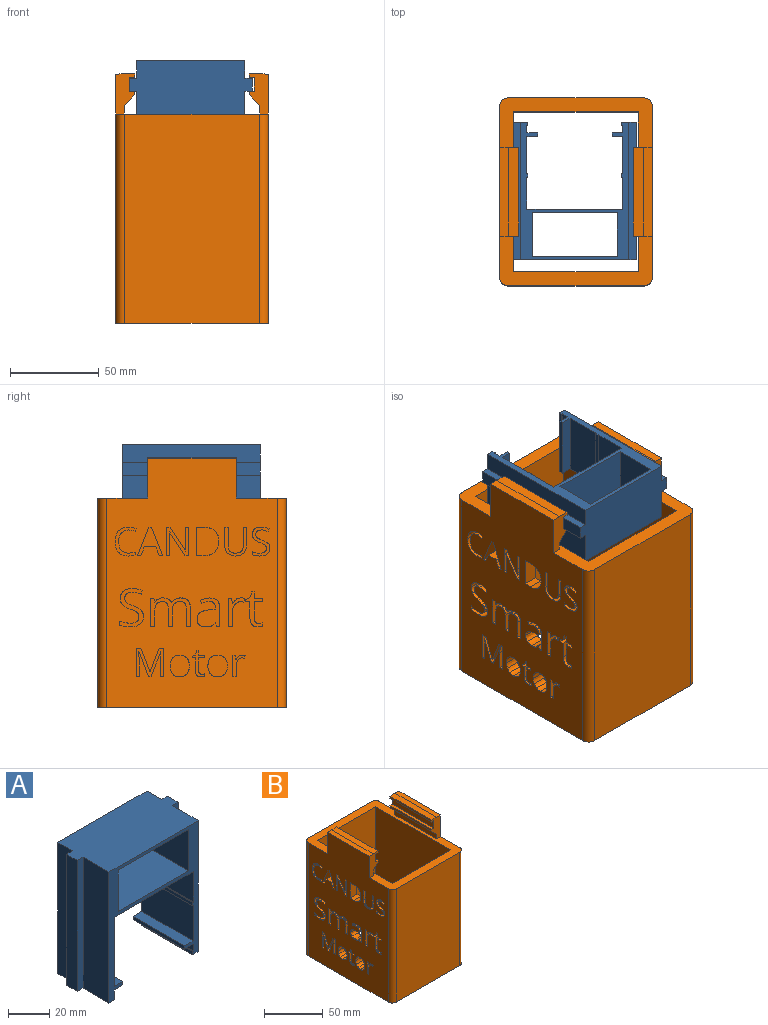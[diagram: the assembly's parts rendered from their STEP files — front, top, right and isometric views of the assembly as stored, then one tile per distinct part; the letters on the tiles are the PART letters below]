
ASSEMBLY  parts=2 mates=2
PART A: 42 faces, bbox 69x35x77.5 mm
  f0: plane 77.5x10mm, normal (1,0,0), area 775mm2, adj f16,f18,f35,f41
  f1: plane 77.5x10mm, normal (-1,0,0), area 775mm2, adj f18,f20,f35,f37
  f2: plane 35x0.5mm, normal (0,0,1), area 17.5mm2, adj f3,f33,f34,f35
  f3: plane 35x18mm, normal (1,0,0), area 630mm2, adj f2,f4,f34,f35
  f4: plane 54x35mm, normal (0,0,-1), area 1890mm2, adj f3,f5,f34,f35
  f5: plane 35x18mm, normal (-1,0,0), area 630mm2, adj f4,f6,f34,f35
  f6: plane 35x0.5mm, normal (0,0,1), area 17.5mm2, adj f5,f7,f34,f35
  f7: plane 35x2mm, normal (-1,0,0), area 70mm2, adj f6,f8,f34,f35
  f8: plane 35x0.5mm, normal (0,0,-1), area 17.5mm2, adj f7,f9,f34,f35
  f9: plane 35x21mm, normal (-1,0,0), area 735mm2, adj f8,f10,f34,f35
  f10: plane 35x6mm, normal (0,0,1), area 210mm2, adj f9,f11,f34,f35
  f11: plane 35x2mm, normal (-1,0,0), area 70mm2, adj f10,f12,f34,f35
  f12: plane 35x6mm, normal (0,0,-1), area 210mm2, adj f11,f13,f34,f35
  f13: plane 35x4mm, normal (-1,0,0), area 140mm2, adj f12,f14,f34,f35
  f14: plane 35x0.5mm, normal (0,0,1), area 17.5mm2, adj f13,f15,f34,f35
  f15: plane 35x2mm, normal (-1,0,0), area 70mm2, adj f14,f16,f34,f35
  f16: plane 35x8mm, normal (0,0,-1), area 169.2mm2, adj f0,f15,f17,f34,f35,f39,f40,f41
  f17: plane 77.5x17.7mm, normal (1,0,0), area 1371.8mm2, adj f16,f18,f34,f39
  f18: plane 69x35mm, normal (0,0,1), area 2193.4mm2, adj f0,f1,f17,f19,f34,f35,f36,f37
  f19: plane 77.5x17.7mm, normal (-1,0,0), area 1371.8mm2, adj f18,f20,f34,f36
  f20: plane 35x8mm, normal (0,0,-1), area 169.2mm2, adj f1,f19,f21,f34,f35,f36,f37,f38
  f21: plane 35x2mm, normal (1,0,0), area 70mm2, adj f20,f22,f34,f35
  f22: plane 35x0.5mm, normal (0,0,1), area 17.5mm2, adj f21,f23,f34,f35
  f23: plane 35x4mm, normal (1,0,0), area 140mm2, adj f22,f24,f34,f35
  f24: plane 35x6mm, normal (0,0,-1), area 210mm2, adj f23,f25,f34,f35
  f25: plane 35x2mm, normal (1,0,0), area 70mm2, adj f24,f26,f34,f35
  f26: plane 35x6mm, normal (0,0,1), area 210mm2, adj f25,f27,f34,f35
  f27: plane 35x21mm, normal (1,0,0), area 735mm2, adj f26,f28,f34,f35
  f28: plane 35x0.5mm, normal (0,0,-1), area 17.5mm2, adj f27,f33,f34,f35
  f29: plane 35x24.5mm, normal (-1,0,0), area 857.5mm2, adj f30,f32,f34,f35
  f30: plane 48x35mm, normal (0,0,1), area 1680mm2, adj f29,f31,f34,f35
  f31: plane 35x24.5mm, normal (1,0,0), area 857.5mm2, adj f30,f32,f34,f35
  f32: plane 48x35mm, normal (0,0,-1), area 1680mm2, adj f29,f31,f34,f35
  f33: plane 35x2mm, normal (1,0,0), area 70mm2, adj f2,f28,f34,f35
  f34: plane 77.5x61mm, normal (0,-1,0), area 933.5mm2, adj f2,f3,f4,f5,f6,f7,f8,f9
  f35: plane 77.5x61mm, normal (0,1,0), area 933.5mm2, adj f0,f1,f2,f3,f4,f5,f6,f7
  f36: plane 77.5x4mm, normal (0,-1,0), area 310mm2, adj f18,f19,f20,f38
  f37: plane 77.5x4mm, normal (0,1,0), area 310mm2, adj f1,f18,f20,f38
  f38: plane 77.5x7.3mm, normal (-1,0,0), area 565.8mm2, adj f18,f20,f36,f37
  f39: plane 77.5x4mm, normal (0,-1,0), area 310mm2, adj f16,f17,f18,f40
  f40: plane 77.5x7.3mm, normal (1,0,0), area 565.7mm2, adj f16,f18,f39,f41
  f41: plane 77.5x4mm, normal (0,1,0), area 310mm2, adj f0,f16,f18,f40
PART B: 292 faces, bbox 86x106x140.6 mm
  f0: plane 140.5x96mm, normal (-1,0,0), area 11035.3mm2, adj f2,f4,f5,f13,f29,f32,f33,f36
  f1: plane 118x90mm, normal (1,0,0), area 9202.5mm2, adj f2,f10,f11,f13,f36,f37,f38,f39
  f2: plane 106x86mm, normal (0,0,1), area 2309.5mm2, adj f0,f1,f3,f4,f5,f6,f7,f8
  f3: plane 118x76mm, normal (0,1,0), area 8968mm2, adj f2,f4,f12,f13
  f4: cylinder r=5mm len=118mm, axis (0,0,-1), area 926.8mm2, adj f0,f2,f3,f13
  f5: cylinder r=5mm len=118mm, axis (0,0,-1), area 926.8mm2, adj f0,f2,f6,f13
  f6: plane 118x76mm, normal (0,-1,0), area 8968mm2, adj f2,f5,f7,f13
  f7: cylinder r=5mm len=118mm, axis (0,0,-1), area 926.8mm2, adj f2,f6,f8,f13
  f8: plane 140.5x96mm, normal (1,0,0), area 12452.8mm2, adj f2,f7,f12,f13,f16,f22,f23
  f9: plane 118x90mm, normal (-1,0,0), area 10620mm2, adj f2,f10,f11,f13
  f10: plane 118x70mm, normal (0,1,0), area 8260mm2, adj f1,f2,f9,f13
  f11: plane 118x70mm, normal (0,-1,0), area 8260mm2, adj f1,f2,f9,f13
  f12: cylinder r=5mm len=118mm, axis (0,0,-1), area 926.8mm2, adj f2,f3,f8,f13
  f13: plane 106x86mm, normal (0,0,-1), area 2794.5mm2, adj f0,f1,f3,f4,f5,f6,f7,f8
  f14: plane 50x2mm, normal (-1,0,0), area 100mm2, adj f21,f22,f23,f34
  f15: plane 50x4.8mm, normal (-1,0,0), area 240mm2, adj f2,f22,f23,f34
  f16: plane 50x4.85mm, normal (0.02,0,1), area 242.6mm2, adj f8,f17,f22,f23
  f17: plane 50x6mm, normal (0,0,1), area 300mm2, adj f16,f18,f22,f23
  f18: plane 50x2mm, normal (-1,0,0), area 100mm2, adj f17,f19,f22,f23
  f19: plane 50x3mm, normal (0,0,-1), area 150mm2, adj f18,f20,f22,f23
  f20: plane 50x7.8mm, normal (-1,0,0), area 390mm2, adj f19,f21,f22,f23
  f21: plane 50x3mm, normal (0,0,1), area 150mm2, adj f14,f20,f22,f23
  f22: plane 22.6x10.85mm, normal (0,-1,0), area 174.8mm2, adj f2,f8,f14,f15,f16,f17,f18,f19
  f23: plane 22.6x10.85mm, normal (0,1,0), area 174.8mm2, adj f2,f8,f14,f15,f16,f17,f18,f19
  f24: plane 50x3mm, normal (0,0,1), area 150mm2, adj f25,f31,f32,f33
  f25: plane 50x7.8mm, normal (1,0,0), area 390mm2, adj f24,f26,f32,f33
  f26: plane 50x3mm, normal (0,0,-1), area 150mm2, adj f25,f27,f32,f33
  f27: plane 50x2mm, normal (1,0,0), area 100mm2, adj f26,f28,f32,f33
  f28: plane 50x6mm, normal (0,0,1), area 300mm2, adj f27,f29,f32,f33
  f29: plane 50x4.85mm, normal (-0.02,0,1), area 242.6mm2, adj f0,f28,f32,f33
  f30: plane 50x4.8mm, normal (1,0,0), area 240mm2, adj f2,f32,f33,f35
  f31: plane 50x2mm, normal (1,0,0), area 100mm2, adj f24,f32,f33,f35
  f32: plane 22.6x10.85mm, normal (0,-1,0), area 174.8mm2, adj f0,f2,f24,f25,f26,f27,f28,f29
  f33: plane 22.6x10.85mm, normal (0,1,0), area 174.8mm2, adj f0,f2,f24,f25,f26,f27,f28,f29
  f34: plane 50x6mm, normal (-0.71,0,-0.71), area 424.3mm2, adj f14,f15,f22,f23
  f35: plane 50x6mm, normal (0.71,0,-0.71), area 424.3mm2, adj f30,f31,f32,f33
  f36: extruded ~8x4.14mm, area 37.1mm2, adj f0,f1,f37,f50
  f37: extruded ~8x3.61mm, area 29.9mm2, adj f0,f1,f36,f38
  f38: plane 8x1.59mm, normal (0,0.9,0.44), area 14.2mm2, adj f0,f1,f37,f39
  f39: extruded ~8x4.37mm, area 36mm2, adj f0,f1,f38,f40
  f40: extruded ~8x4.08mm, area 34mm2, adj f0,f1,f39,f41
  f41: extruded ~8x2.85mm, area 31.6mm2, adj f0,f1,f40,f42
  f42: extruded ~8x4.31mm, area 35.5mm2, adj f0,f1,f41,f43
  f43: extruded ~8x6.06mm, area 52mm2, adj f0,f1,f42,f44
  f44: extruded ~8x5.42mm, area 48.1mm2, adj f0,f1,f43,f45
  f45: extruded ~8x4.08mm, area 33.2mm2, adj f0,f1,f44,f46
  f46: plane 8x1.62mm, normal (0,1,0), area 12.9mm2, adj f0,f1,f45,f47
  f47: extruded ~8x3.8mm, area 30.8mm2, adj f0,f1,f46,f48
  f48: extruded ~8x4.17mm, area 37.3mm2, adj f0,f1,f47,f49
  f49: extruded ~8x4.82mm, area 41.2mm2, adj f0,f1,f48,f50
  f50: extruded ~8x4.78mm, area 41mm2, adj f0,f1,f36,f49
  f51: extruded ~8x0.93mm, area 7.4mm2, adj f0,f1,f52,f69
  f52: extruded ~8x1.4mm, area 12.5mm2, adj f0,f1,f51,f53
  f53: extruded ~8x1.65mm, area 14.1mm2, adj f0,f1,f52,f54
  f54: plane 8x7.01mm, normal (0,1,0), area 56.1mm2, adj f0,f1,f53,f55
  f55: plane 8x3.46mm, normal (0,0,1), area 27.7mm2, adj f0,f1,f54,f56
  f56: plane 8x1.4mm, normal (0,1,0), area 11.2mm2, adj f0,f1,f55,f57
  f57: plane 8x3.46mm, normal (0,0,-1), area 27.7mm2, adj f0,f1,f56,f58
  f58: plane 8x2.76mm, normal (0,1,0), area 22.1mm2, adj f0,f1,f57,f59
  f59: plane 8x1.04mm, normal (0,0,-1), area 8.3mm2, adj f0,f1,f58,f60
  f60: plane 8x2.54mm, normal (0,-0.96,-0.29), area 21.2mm2, adj f0,f1,f59,f61
  f61: plane 8x1.71mm, normal (0,-0.4,-0.92), area 14.9mm2, adj f0,f1,f60,f62
  f62: plane 8x0.87mm, normal (0,-1,0), area 7mm2, adj f0,f1,f61,f63
  f63: plane 8x1.71mm, normal (0,0,1), area 13.7mm2, adj f0,f1,f62,f64
  f64: plane 8x7.09mm, normal (0,-1,0), area 56.7mm2, adj f0,f1,f63,f65
  f65: extruded ~8x3.64mm, area 46.1mm2, adj f0,f1,f64,f66
  f66: extruded ~8x1.03mm, area 8.3mm2, adj f0,f1,f65,f67
  f67: extruded ~8x0.86mm, area 7.2mm2, adj f0,f1,f66,f68
  f68: plane 8x1.38mm, normal (0,1,0), area 11mm2, adj f0,f1,f67,f69
  f69: extruded ~8x0.71mm, area 5.8mm2, adj f0,f1,f51,f68
  f70: extruded ~8x1.42mm, area 11.5mm2, adj f0,f1,f71,f82
  f71: extruded ~8x2.06mm, area 17.5mm2, adj f0,f1,f70,f72
  f72: extruded ~8x1.79mm, area 19.4mm2, adj f0,f1,f71,f73
  f73: plane 8x0.09mm, normal (0,0,-1), area 0.7mm2, adj f0,f1,f72,f74
  f74: plane 8x2.21mm, normal (0,1,-0.09), area 17.7mm2, adj f0,f1,f73,f75
  f75: plane 8x1.49mm, normal (0,0,-1), area 11.9mm2, adj f0,f1,f74,f76
  f76: plane 11.91x8mm, normal (0,-1,0), area 95.3mm2, adj f0,f1,f75,f77
  f77: plane 8x1.81mm, normal (0,0,1), area 14.4mm2, adj f0,f1,f76,f78
  f78: plane 8x6.39mm, normal (0,1,0), area 51.2mm2, adj f0,f1,f77,f79
  f79: extruded ~8x2.92mm, area 25.4mm2, adj f0,f1,f78,f80
  f80: extruded ~8x2.47mm, area 22.6mm2, adj f0,f1,f79,f81
  f81: extruded ~8x1.3mm, area 10.5mm2, adj f0,f1,f80,f82
  f82: plane 8x1.67mm, normal (0,0.99,0.15), area 13.5mm2, adj f0,f1,f70,f81
  f83: plane 8x5.06mm, normal (0,-0.93,0.36), area 43.4mm2, adj f0,f1,f84,f90
  f84: plane 8x1.91mm, normal (0,0,1), area 15.3mm2, adj f0,f1,f83,f85
  f85: plane 15.97x8mm, normal (0,0.93,-0.36), area 137.2mm2, adj f0,f1,f84,f86
  f86: plane 8x1.56mm, normal (0,0,-1), area 12.4mm2, adj f0,f1,f85,f87
  f87: plane 15.97x8mm, normal (0,-0.93,-0.37), area 137.3mm2, adj f0,f1,f86,f88
  f88: plane 8x1.87mm, normal (0,0,1), area 15mm2, adj f0,f1,f87,f89
  f89: plane 8x5.06mm, normal (0,0.93,0.36), area 43.4mm2, adj f0,f1,f88,f90
  f90: plane 8x6.37mm, normal (0,0,1), area 51mm2, adj f0,f1,f83,f89
  f91: extruded ~8x6.02mm, area 52.5mm2, adj f0,f1,f92,f97
  f92: extruded ~8x5.74mm, area 50.1mm2, adj f0,f1,f91,f93
  f93: extruded ~8x5.77mm, area 50.3mm2, adj f0,f1,f92,f94
  f94: plane 8x4.87mm, normal (0,0,-1), area 39mm2, adj f0,f1,f93,f95
  f95: plane 15.9x8mm, normal (0,-1,0), area 127.2mm2, adj f0,f1,f94,f96
  f96: plane 8x4.41mm, normal (0,0,1), area 35.2mm2, adj f0,f1,f95,f97
  f97: extruded ~8x6.15mm, area 53.3mm2, adj f0,f1,f91,f96
  f98: extruded ~8x4.55mm, area 39.1mm2, adj f0,f1,f99,f106
  f99: extruded ~8x4.5mm, area 38.7mm2, adj f0,f1,f98,f100
  f100: extruded ~8x3.97mm, area 35.6mm2, adj f0,f1,f99,f101
  f101: extruded ~8x4.05mm, area 36mm2, adj f0,f1,f100,f102
  f102: extruded ~8x4.54mm, area 39mm2, adj f0,f1,f101,f103
  f103: extruded ~8x3.28mm, area 27mm2, adj f0,f1,f102,f104
  f104: extruded ~8x2.15mm, area 23.4mm2, adj f0,f1,f103,f105
  f105: extruded ~8x2.84mm, area 23.8mm2, adj f0,f1,f104,f106
  f106: extruded ~8x4.05mm, area 36.1mm2, adj f0,f1,f98,f105
  f107: extruded ~8x4.55mm, area 39.1mm2, adj f0,f1,f108,f115
  f108: extruded ~8x4.5mm, area 38.7mm2, adj f0,f1,f107,f109
  f109: extruded ~8x3.97mm, area 35.6mm2, adj f0,f1,f108,f110
  f110: extruded ~8x4.05mm, area 36mm2, adj f0,f1,f109,f111
  f111: extruded ~8x4.54mm, area 39mm2, adj f0,f1,f110,f112
  f112: extruded ~8x3.28mm, area 27mm2, adj f0,f1,f111,f113
  f113: extruded ~8x2.15mm, area 23.4mm2, adj f0,f1,f112,f114
  f114: extruded ~8x2.84mm, area 23.8mm2, adj f0,f1,f113,f115
  f115: extruded ~8x4.05mm, area 36.1mm2, adj f0,f1,f107,f114
  f116: plane 8x2.25mm, normal (0,-0.98,0.21), area 18.4mm2, adj f0,f1,f117,f134
  f117: plane 8x1.78mm, normal (0,0,1), area 14.2mm2, adj f0,f1,f116,f118
  f118: plane 10.79x8mm, normal (0,1,0), area 86.3mm2, adj f0,f1,f117,f119
  f119: extruded ~8x4.02mm, area 35mm2, adj f0,f1,f118,f120
  f120: extruded ~8x4.19mm, area 35.8mm2, adj f0,f1,f119,f121
  f121: extruded ~8x2.79mm, area 22.6mm2, adj f0,f1,f120,f122
  f122: extruded ~8x2.56mm, area 22mm2, adj f0,f1,f121,f123
  f123: plane 8x1.83mm, normal (0,-0.93,0.37), area 15.8mm2, adj f0,f1,f122,f124
  f124: extruded ~8x4.47mm, area 37.3mm2, adj f0,f1,f123,f125
  f125: extruded ~8x2.56mm, area 22.3mm2, adj f0,f1,f124,f126
  f126: extruded ~8x2.75mm, area 23.4mm2, adj f0,f1,f125,f127
  f127: plane 8x0.98mm, normal (0,-1,0), area 7.9mm2, adj f0,f1,f126,f128
  f128: plane 8x2.68mm, normal (0,-0.03,-1), area 21.5mm2, adj f0,f1,f127,f129
  f129: extruded ~8x7.65mm, area 82.3mm2, adj f0,f1,f128,f130
  f130: extruded ~8x3.45mm, area 30.5mm2, adj f0,f1,f129,f131
  f131: extruded ~8x3.68mm, area 31.7mm2, adj f0,f1,f130,f132
  f132: extruded ~8x2.94mm, area 24mm2, adj f0,f1,f131,f133
  f133: extruded ~8x2.36mm, area 25mm2, adj f0,f1,f132,f134
  f134: plane 8x0.12mm, normal (0,0,1), area 0.9mm2, adj f0,f1,f116,f133
  f135: extruded ~8x4.34mm, area 39.8mm2, adj f0,f1,f136,f159
  f136: extruded ~8x3.52mm, area 30.6mm2, adj f0,f1,f135,f137
  f137: extruded ~8x4.56mm, area 42.1mm2, adj f0,f1,f136,f138
  f138: extruded ~8x2.93mm, area 25.7mm2, adj f0,f1,f137,f139
  f139: extruded ~8x1.36mm, area 15.1mm2, adj f0,f1,f138,f140
  f140: extruded ~8x1.79mm, area 14.9mm2, adj f0,f1,f139,f141
  f141: extruded ~8x2.32mm, area 21.3mm2, adj f0,f1,f140,f142
  f142: extruded ~8x3.04mm, area 25.7mm2, adj f0,f1,f141,f143
  f143: extruded ~8x5.08mm, area 41.8mm2, adj f0,f1,f142,f144
  f144: plane 8x2.13mm, normal (0,0.94,0.34), area 18.1mm2, adj f0,f1,f143,f145
  f145: extruded ~8x5.78mm, area 47.5mm2, adj f0,f1,f144,f146
  f146: extruded ~8x4.85mm, area 41.2mm2, adj f0,f1,f145,f147
  f147: extruded ~8x3.88mm, area 35.6mm2, adj f0,f1,f146,f148
  f148: extruded ~8x3.76mm, area 32.5mm2, adj f0,f1,f147,f149
  f149: extruded ~8x4.2mm, area 39.5mm2, adj f0,f1,f148,f150
  f150: extruded ~8x3.14mm, area 27.3mm2, adj f0,f1,f149,f151
  f151: extruded ~8x1.47mm, area 15.8mm2, adj f0,f1,f150,f152
  f152: extruded ~8x1.79mm, area 15mm2, adj f0,f1,f151,f153
  f153: extruded ~8x2.59mm, area 23.9mm2, adj f0,f1,f152,f154
  f154: extruded ~8x3.69mm, area 31mm2, adj f0,f1,f153,f155
  f155: extruded ~8x3.03mm, area 24.4mm2, adj f0,f1,f154,f156
  f156: extruded ~8x2.83mm, area 23.7mm2, adj f0,f1,f155,f157
  f157: plane 8x2.36mm, normal (0,-1,0), area 18.9mm2, adj f0,f1,f156,f158
  f158: extruded ~8x5.77mm, area 47.1mm2, adj f0,f1,f157,f159
  f159: extruded ~8x5.48mm, area 46.4mm2, adj f0,f1,f135,f158
  f160: extruded ~8x3.28mm, area 30mm2, adj f0,f1,f161,f184
  f161: extruded ~8x2.65mm, area 23.1mm2, adj f0,f1,f160,f162
  f162: extruded ~8x3.44mm, area 31.8mm2, adj f0,f1,f161,f163
  f163: extruded ~8x2.21mm, area 19.4mm2, adj f0,f1,f162,f164
  f164: extruded ~8x1.03mm, area 11.4mm2, adj f0,f1,f163,f165
  f165: extruded ~8x1.35mm, area 11.2mm2, adj f0,f1,f164,f166
  f166: extruded ~8x1.75mm, area 16.1mm2, adj f0,f1,f165,f167
  f167: extruded ~8x2.3mm, area 19.4mm2, adj f0,f1,f166,f168
  f168: extruded ~8x3.83mm, area 31.5mm2, adj f0,f1,f167,f169
  f169: plane 8x1.61mm, normal (0,0.94,0.34), area 13.7mm2, adj f0,f1,f168,f170
  f170: extruded ~8x4.36mm, area 35.8mm2, adj f0,f1,f169,f171
  f171: extruded ~8x3.66mm, area 31.1mm2, adj f0,f1,f170,f172
  f172: extruded ~8x2.93mm, area 26.9mm2, adj f0,f1,f171,f173
  f173: extruded ~8x2.84mm, area 24.5mm2, adj f0,f1,f172,f174
  f174: extruded ~8x3.17mm, area 29.8mm2, adj f0,f1,f173,f175
  f175: extruded ~8x2.37mm, area 20.6mm2, adj f0,f1,f174,f176
  f176: extruded ~8x1.11mm, area 11.9mm2, adj f0,f1,f175,f177
  f177: extruded ~8x1.35mm, area 11.3mm2, adj f0,f1,f176,f178
  f178: extruded ~8x1.95mm, area 18mm2, adj f0,f1,f177,f179
  f179: extruded ~8x2.78mm, area 23.4mm2, adj f0,f1,f178,f180
  f180: extruded ~8x2.28mm, area 18.4mm2, adj f0,f1,f179,f181
  f181: extruded ~8x2.13mm, area 17.9mm2, adj f0,f1,f180,f182
  f182: plane 8x1.78mm, normal (0,-1,0), area 14.3mm2, adj f0,f1,f181,f183
  f183: extruded ~8x4.35mm, area 35.6mm2, adj f0,f1,f182,f184
  f184: extruded ~8x4.13mm, area 35mm2, adj f0,f1,f160,f183
  f185: plane 10.29x8mm, normal (0,1,0), area 82.3mm2, adj f0,f1,f186,f198
  f186: plane 8x1.85mm, normal (0,0,-1), area 14.8mm2, adj f0,f1,f185,f187
  f187: plane 10.35x8mm, normal (0,-1,0), area 82.8mm2, adj f0,f1,f186,f188
  f188: extruded ~8x3.07mm, area 26.8mm2, adj f0,f1,f187,f189
  f189: extruded ~8x3.1mm, area 26.9mm2, adj f0,f1,f188,f190
  f190: extruded ~8x3.2mm, area 27.7mm2, adj f0,f1,f189,f191
  f191: extruded ~8x3.06mm, area 26.7mm2, adj f0,f1,f190,f192
  f192: plane 10.38x8mm, normal (0,1,0), area 83mm2, adj f0,f1,f191,f193
  f193: plane 8x1.85mm, normal (0,0,-1), area 14.8mm2, adj f0,f1,f192,f194
  f194: plane 10.25x8mm, normal (0,-1,0), area 82mm2, adj f0,f1,f193,f195
  f195: extruded ~8x4.31mm, area 37.7mm2, adj f0,f1,f194,f196
  f196: extruded ~8x4.44mm, area 38.7mm2, adj f0,f1,f195,f197
  f197: extruded ~8x4.51mm, area 39.2mm2, adj f0,f1,f196,f198
  f198: extruded ~8x4.28mm, area 37.7mm2, adj f0,f1,f185,f197
  f199: plane 8x2.11mm, normal (0,0,1), area 16.9mm2, adj f0,f1,f200,f213
  f200: plane 15.9x8mm, normal (0,1,0), area 127.2mm2, adj f0,f1,f199,f201
  f201: plane 8x1.73mm, normal (0,0,-1), area 13.8mm2, adj f0,f1,f200,f202
  f202: plane 9.13x8mm, normal (0,-1,0), area 73mm2, adj f0,f1,f201,f203
  f203: extruded ~8x2.28mm, area 18.2mm2, adj f0,f1,f202,f204
  f204: extruded ~8x1.89mm, area 15.1mm2, adj f0,f1,f203,f205
  f205: plane 8x0.09mm, normal (0,0,-1), area 0.7mm2, adj f0,f1,f204,f206
  f206: plane 13.29x8.67mm, normal (0,0.84,-0.55), area 127mm2, adj f0,f1,f205,f207
  f207: plane 8x2.09mm, normal (0,0,-1), area 16.7mm2, adj f0,f1,f206,f208
  f208: plane 15.9x8mm, normal (0,-1,0), area 127.2mm2, adj f0,f1,f207,f209
  f209: plane 8x1.71mm, normal (0,0,1), area 13.7mm2, adj f0,f1,f208,f210
  f210: plane 9.04x8mm, normal (0,1,0), area 72.3mm2, adj f0,f1,f209,f211
  f211: extruded ~8x4.31mm, area 34.5mm2, adj f0,f1,f210,f212
  f212: plane 8x0.09mm, normal (0,0,1), area 0.7mm2, adj f0,f1,f211,f213
  f213: plane 13.34x8.69mm, normal (0,-0.84,0.55), area 127.4mm2, adj f0,f1,f199,f212
  f214: plane 14.09x8mm, normal (0,-0.93,0.36), area 120.7mm2, adj f0,f1,f215,f231
  f215: plane 8x1.49mm, normal (0,0,1), area 11.9mm2, adj f0,f1,f214,f216
  f216: plane 14.07x8mm, normal (0,0.93,0.36), area 120.7mm2, adj f0,f1,f215,f217
  f217: plane 8x0.09mm, normal (0,0,1), area 0.7mm2, adj f0,f1,f216,f218
  f218: extruded ~8x3.83mm, area 30.6mm2, adj f0,f1,f217,f219
  f219: plane 10.24x8mm, normal (0,-1,0), area 81.9mm2, adj f0,f1,f218,f220
  f220: plane 8x1.85mm, normal (0,0,1), area 14.8mm2, adj f0,f1,f219,f221
  f221: plane 15.89x8mm, normal (0,1,0), area 127.2mm2, adj f0,f1,f220,f222
  f222: plane 8x2.76mm, normal (0,0,-1), area 22.1mm2, adj f0,f1,f221,f223
  f223: plane 13.11x8mm, normal (0,-0.93,-0.36), area 112.5mm2, adj f0,f1,f222,f224
  f224: plane 8x0.09mm, normal (0,0,-1), area 0.7mm2, adj f0,f1,f223,f225
  f225: plane 13.11x8mm, normal (0,0.93,-0.36), area 112.4mm2, adj f0,f1,f224,f226
  f226: plane 8x2.78mm, normal (0,0,-1), area 22.3mm2, adj f0,f1,f225,f227
  f227: plane 15.89x8mm, normal (0,-1,0), area 127.2mm2, adj f0,f1,f226,f228
  f228: plane 8x1.71mm, normal (0,0,1), area 13.7mm2, adj f0,f1,f227,f229
  f229: plane 10.11x8mm, normal (0,1,0), area 80.9mm2, adj f0,f1,f228,f230
  f230: extruded ~8x3.98mm, area 31.9mm2, adj f0,f1,f229,f231
  f231: plane 8x0.09mm, normal (0,0,1), area 0.7mm2, adj f0,f1,f214,f230
  f232: extruded ~8x1.23mm, area 9.9mm2, adj f0,f1,f233,f250
  f233: extruded ~8x1.86mm, area 16.6mm2, adj f0,f1,f232,f234
  f234: extruded ~8x2.19mm, area 18.7mm2, adj f0,f1,f233,f235
  f235: plane 9.3x8mm, normal (0,1,0), area 74.4mm2, adj f0,f1,f234,f236
  f236: plane 8x4.59mm, normal (0,0,1), area 36.7mm2, adj f0,f1,f235,f237
  f237: plane 8x1.86mm, normal (0,1,0), area 14.9mm2, adj f0,f1,f236,f238
  f238: plane 8x4.59mm, normal (0,0,-1), area 36.7mm2, adj f0,f1,f237,f239
  f239: plane 8x3.66mm, normal (0,1,0), area 29.3mm2, adj f0,f1,f238,f240
  f240: plane 8x1.38mm, normal (0,0,-1), area 11.1mm2, adj f0,f1,f239,f241
  f241: plane 8x3.37mm, normal (0,-0.96,-0.29), area 28.2mm2, adj f0,f1,f240,f242
  f242: plane 8x2.27mm, normal (0,-0.4,-0.92), area 19.8mm2, adj f0,f1,f241,f243
  f243: plane 8x1.15mm, normal (0,-1,0), area 9.2mm2, adj f0,f1,f242,f244
  f244: plane 8x2.27mm, normal (0,0,1), area 18.1mm2, adj f0,f1,f243,f245
  f245: plane 9.4x8mm, normal (0,-1,0), area 75.2mm2, adj f0,f1,f244,f246
  f246: extruded ~8x4.83mm, area 61.1mm2, adj f0,f1,f245,f247
  f247: extruded ~8x1.37mm, area 11mm2, adj f0,f1,f246,f248
  f248: extruded ~8x1.14mm, area 9.5mm2, adj f0,f1,f247,f249
  f249: plane 8x1.83mm, normal (0,1,0), area 14.7mm2, adj f0,f1,f248,f250
  f250: extruded ~8x0.94mm, area 7.7mm2, adj f0,f1,f232,f249
  f251: extruded ~8x1.89mm, area 15.2mm2, adj f0,f1,f252,f263
  f252: extruded ~8x2.73mm, area 23.2mm2, adj f0,f1,f251,f253
  f253: extruded ~8x2.38mm, area 25.7mm2, adj f0,f1,f252,f254
  f254: plane 8x0.12mm, normal (0,0,-1), area 0.9mm2, adj f0,f1,f253,f255
  f255: plane 8x2.93mm, normal (0,1,-0.09), area 23.5mm2, adj f0,f1,f254,f256
  f256: plane 8x1.97mm, normal (0,0,-1), area 15.8mm2, adj f0,f1,f255,f257
  f257: plane 15.8x8mm, normal (0,-1,0), area 126.4mm2, adj f0,f1,f256,f258
  f258: plane 8x2.39mm, normal (0,0,1), area 19.2mm2, adj f0,f1,f257,f259
  f259: plane 8.48x8mm, normal (0,1,0), area 67.8mm2, adj f0,f1,f258,f260
  f260: extruded ~8x3.88mm, area 33.6mm2, adj f0,f1,f259,f261
  f261: extruded ~8x3.28mm, area 30mm2, adj f0,f1,f260,f262
  f262: extruded ~8x1.73mm, area 14mm2, adj f0,f1,f261,f263
  f263: plane 8x2.22mm, normal (0,0.99,0.15), area 18mm2, adj f0,f1,f251,f262
  f264: plane 10.28x8mm, normal (0,-1,0), area 82.2mm2, adj f0,f1,f265,f291
  f265: plane 8x2.39mm, normal (0,0,1), area 19.1mm2, adj f0,f1,f264,f266
  f266: plane 10.31x8mm, normal (0,1,0), area 82.5mm2, adj f0,f1,f265,f267
  f267: extruded ~8x4.41mm, area 37.8mm2, adj f0,f1,f266,f268
  f268: extruded ~8x4.01mm, area 34.9mm2, adj f0,f1,f267,f269
  f269: extruded ~8x3.06mm, area 25.4mm2, adj f0,f1,f268,f270
  f270: extruded ~8x2.05mm, area 23mm2, adj f0,f1,f269,f271
  f271: plane 8x0.12mm, normal (0,0,-1), area 0.9mm2, adj f0,f1,f270,f272
  f272: extruded ~8x4.84mm, area 47.3mm2, adj f0,f1,f271,f273
  f273: extruded ~8x2.76mm, area 22.9mm2, adj f0,f1,f272,f274
  f274: extruded ~8x1.91mm, area 21.3mm2, adj f0,f1,f273,f275
  f275: plane 8x0.12mm, normal (0,0,-1), area 0.9mm2, adj f0,f1,f274,f276
  f276: plane 8x2.16mm, normal (0,0.98,-0.18), area 17.6mm2, adj f0,f1,f275,f277
  f277: plane 8x1.95mm, normal (0,0,-1), area 15.6mm2, adj f0,f1,f276,f278
  f278: plane 15.8x8mm, normal (0,-1,0), area 126.4mm2, adj f0,f1,f277,f279
  f279: plane 8x2.39mm, normal (0,0,1), area 19.2mm2, adj f0,f1,f278,f280
  f280: plane 8.29x8mm, normal (0,1,0), area 66.3mm2, adj f0,f1,f279,f281
  f281: extruded ~8x4.42mm, area 36.9mm2, adj f0,f1,f280,f282
  f282: extruded ~8x3.29mm, area 29.5mm2, adj f0,f1,f281,f283
  f283: extruded ~8x2.52mm, area 22.3mm2, adj f0,f1,f282,f284
  f284: extruded ~8x2.84mm, area 24.1mm2, adj f0,f1,f283,f285
  f285: plane 10.28x8mm, normal (0,-1,0), area 82.2mm2, adj f0,f1,f284,f286
  f286: plane 8x2.39mm, normal (0,0,1), area 19.2mm2, adj f0,f1,f285,f287
  f287: plane 8.83x8mm, normal (0,1,0), area 70.6mm2, adj f0,f1,f286,f288
  f288: extruded ~8x3.95mm, area 33.4mm2, adj f0,f1,f287,f289
  f289: extruded ~8x3.3mm, area 29.3mm2, adj f0,f1,f288,f290
  f290: extruded ~8x2.51mm, area 22.2mm2, adj f0,f1,f289,f291
  f291: extruded ~8x2.84mm, area 24.1mm2, adj f0,f1,f264,f290
PLACE A rot(axis=(1,0,0),90deg) t=(-31.78,23.17,150.71)mm
PLACE B t=(-23.13,-29.95,12.61)mm fixed
MATE planar A.f36 <-> B.f24  axis (0,0,-1) through (-91.28,15.42,133.41)mm
MATE planar A.f38 <-> B.f25  axis (-1,0,0) through (-93.28,15.42,137.06)mm
